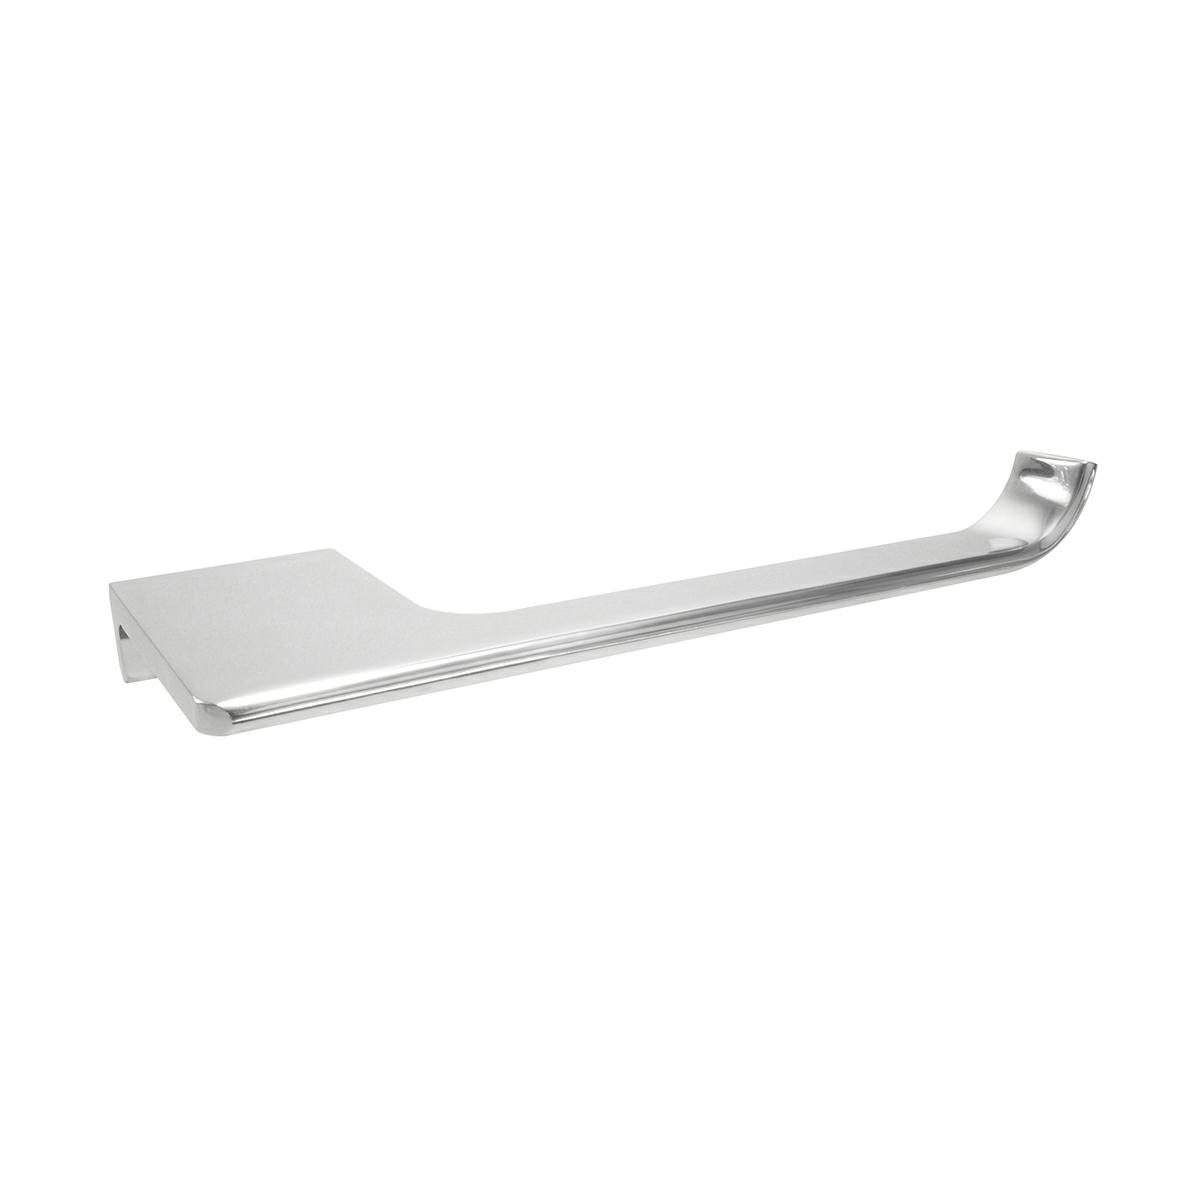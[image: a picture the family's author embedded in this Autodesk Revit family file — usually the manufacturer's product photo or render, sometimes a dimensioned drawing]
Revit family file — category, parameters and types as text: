
# Revit family: ACC-117
name_source: partatom
category: Aparatos sanitarios
units: mm (PartAtom-declared; Revit-internal decimal feet)

## family parameters
Compartido = No
Corte con vacíos al cargar = No
Cota de conector redondo = Diámetro de uso
Número OmniClass = 23.45.00.00
Punto de cálculo de habitación = No
Se basa en plano de trabajo = No
Siempre vertical = Sí
Tipo de pieza = Normal
Título OmniClass = Sanitary, Laundry, and Cleaning Equipment

## types (5) — shared parameters
Brass Chromed = Brass
Comentarios de tipo = Accesories
Elevación por defecto = 0"
Fabricante = HELVEX

## per-type parameters (varying)
| type | Data Sheet | Descripción | Features | Imagen de tipo | Instructive | Total Depth | Total Length | Total Support Diameter | URL | Ébano |
| 14104 | http://helvex.com | Kúbica Paper Holder | Wall Mounted Accessory; Setting Kit Included; Includes Fastening Tool | <Ninguno> | http://helvex.com | 3" | 8" | 2" | http://helvex.com | <Por categoría> |
| ACC-105 | https://www.helvex.com.mx | Toallero de barra Access | Bar towel rack Accessed. | <Ninguno> | https://www.helvex.com.mx | 3" | 24" | 1" | https://www.helvex.com.mx | <Por categoría> |
| ACC-106 | https://www.helvex.com.mx | Gancho sencillo Access | Access simple hook | <Ninguno> | https://www.helvex.com.mx | 3" | 2" | 1" | https://www.helvex.com.mx | <Por categoría> |
| ACC-109 | https://www.helvex.com.mx | Toallero sencillo Access | Accessory single towel rack | <Ninguno> | https://www.helvex.com.mx | 1" | 11" | 1" | https://www.helvex.com.mx | <Por categoría> |
| ACC-117 | https://www.helvex.com.mx | Portapapel Access | Access Paper Holder | ACC-117.jpg | https://www.helvex.com.mx | 1" | 8" | 2" | https://www.helvex.com.mx | Ébano |

note: column(s) folded — value = type name in every type: Modelo

## geometry (parser evidence)
native form markers: Sweep x3
no freeform markers — native parametric forms only
